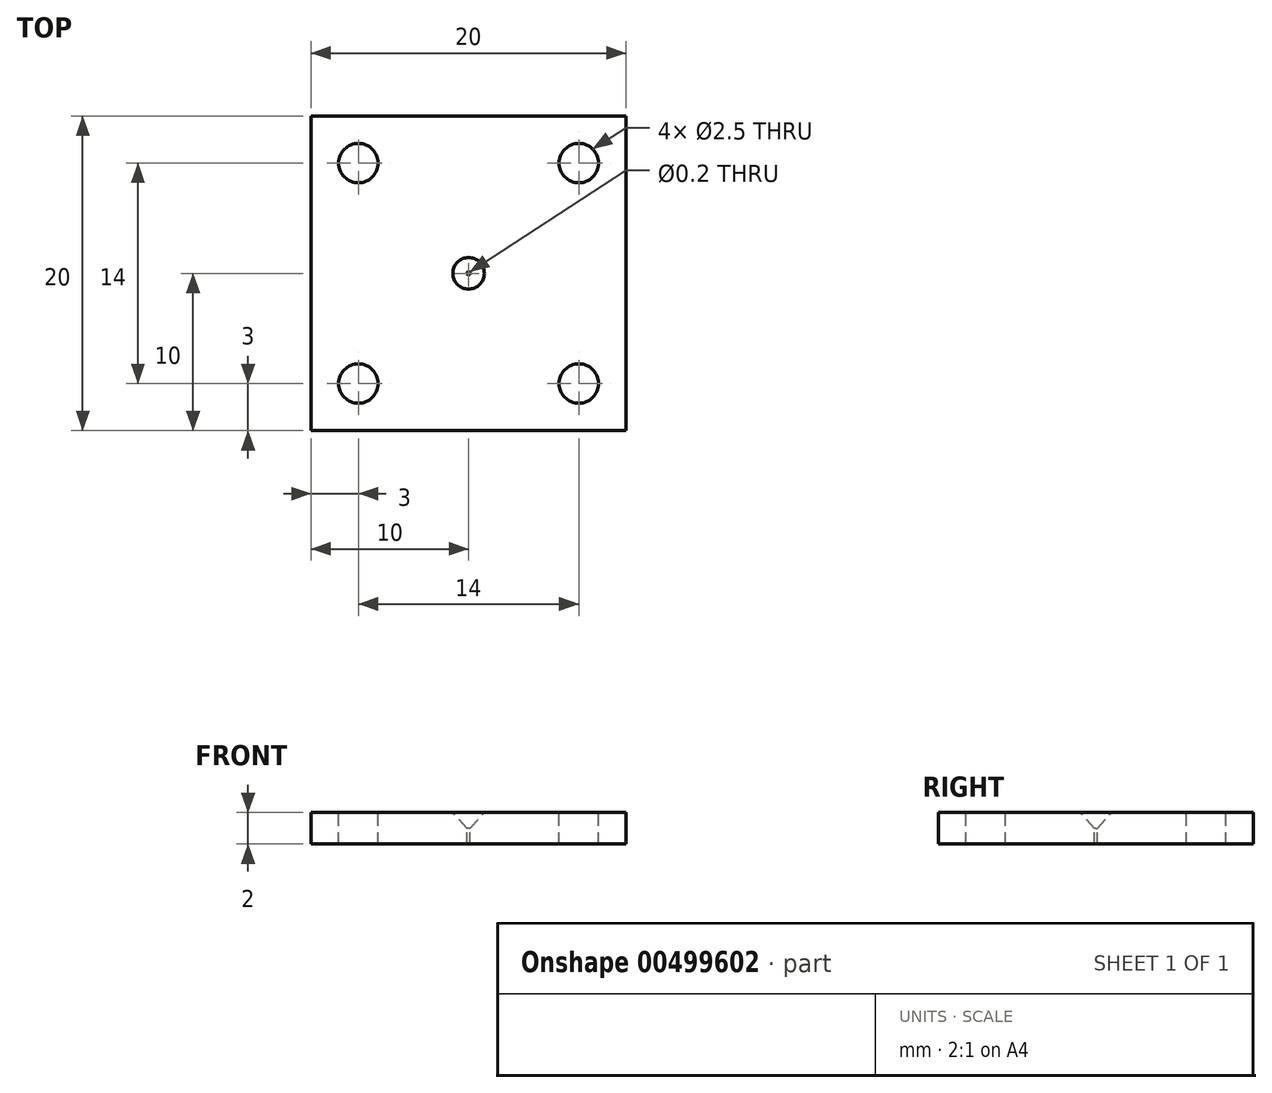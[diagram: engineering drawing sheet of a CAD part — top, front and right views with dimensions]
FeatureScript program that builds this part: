
annotation { "Feature Type Name" : "Feature", "Feature Type Description" : "" }
export const myFeature = defineFeature(function(context is Context, id is Id, definition is map)
    precondition{}
    {
        {
            var Q0;
            Q0=qCreatedBy(makeId("Top.planeOp"),FACE);
            var sketch = newSketch(context, id + "F0", { "sketchPlane" : qUnion([Q0])});
            skLineSegment(sketch, "E0.bottom", {"start": v(-10, 10) * mm, "end": v(10, 10) * mm});
            skLineSegment(sketch, "E0.top", {"start": v(-10, -10) * mm, "end": v(10, -10) * mm});
            skLineSegment(sketch, "E0.left", {"start": v(-10, 10) * mm, "end": v(-10, -10) * mm});
            skLineSegment(sketch, "E0.right", {"start": v(10, 10) * mm, "end": v(10, -10) * mm});
            skSolve(sketch);
        }
        {
            var Q0;
            Q0=makeQuery(id+"F0.imprint","IMPRINT",FACE,{"disambiguationData":[TD([[makeQuery(id+"F0.imprint","IMPRINT",EDGE,{"derivedFrom":sQuery(id+"F0.wireOp",EDGE,"E0.bottom")}),-1.0]])]});
            extrude(context, id + "F1", {"entities" : qUnion([Q0]), "oppositeDirection" : true, "depth" : 1 * mm});
        }
        {
            var Q0;
            Q0=makeQuery(id+"F1.opExtrude","CAP_FACE",FACE,{"disambiguationData":[OSD([sQuery(id+"F0.wireOp",EDGE,"E0.bottom"),sQuery(id+"F0.wireOp",EDGE,"E0.top"),sQuery(id+"F0.wireOp",EDGE,"E0.left"),sQuery(id+"F0.wireOp",EDGE,"E0.right")])],"isStart":true});
            var sketch = newSketch(context, id + "F2", { "sketchPlane" : qUnion([Q0])});
            skCircle(sketch, "E1", {"center": v(0, 0) * mm, "radius": 1 * mm});
            skSolve(sketch);
        }
        {
            var Q0;
            Q0=makeQuery(id+"F1.opExtrude","CAP_FACE",FACE,{"disambiguationData":[OSD([sQuery(id+"F0.wireOp",EDGE,"E0.bottom"),sQuery(id+"F0.wireOp",EDGE,"E0.top"),sQuery(id+"F0.wireOp",EDGE,"E0.left"),sQuery(id+"F0.wireOp",EDGE,"E0.right")])],"isStart":false});
            var sketch = newSketch(context, id + "F3", { "sketchPlane" : qUnion([Q0])});
            skCircle(sketch, "E2", {"center": v(0, 0) * mm, "radius": 0.1 * mm});
            skSolve(sketch);
        }
        {
            var Q1;
            Q1=makeQuery(id+"F2.imprint","IMPRINT",FACE,{"disambiguationData":[TD([[makeQuery(id+"F2.imprint","IMPRINT",EDGE,{"derivedFrom":sQuery(id+"F2.wireOp",EDGE,"E1")}),1.0]])]});
            var Q2;
            Q2=makeQuery(id+"F3.imprint","IMPRINT",FACE,{"disambiguationData":[TD([[makeQuery(id+"F3.imprint","IMPRINT",EDGE,{"derivedFrom":sQuery(id+"F3.wireOp",EDGE,"E2")}),1.0]])]});
            loft(context, id + "F4", {"operationType" : NewBodyOperationType.REMOVE, "sheetProfilesArray" : [{ "sheetProfileEntities" : qUnion([Q1]) }, { "sheetProfileEntities" : qUnion([Q2]) }]});
        }
        {
            var Q0;
            Q0=makeQuery(id+"F2.imprint","IMPRINT",FACE,{"disambiguationData":[TD([[makeQuery(id+"F2.imprint","IMPRINT",EDGE,{"derivedFrom":sQuery(id+"F2.wireOp",EDGE,"E1")}),-1.0]])]});
            var sketch = newSketch(context, id + "F5", { "sketchPlane" : qUnion([Q0])});
            skPoint(sketch, "E3", {"position": v(7, 7) * mm});
            skLineSegment(sketch, "E4", {"start": v(10.77, 0) * mm, "end": v(-10.68, 0) * mm});
            skLineSegment(sketch, "E5", {"start": v(0, -10.66) * mm, "end": v(0, 12.03) * mm});
            skPoint(sketch, "E6.MirrorP", {"position": v(-7, 7) * mm});
            skPoint(sketch, "E7.MirrorP", {"position": v(-7, -7) * mm});
            skPoint(sketch, "E8.MirrorP", {"position": v(7, -7) * mm});
            skSolve(sketch);
        }
        {
            var Q0;
            Q0=makeQuery(id+"F3.imprint","IMPRINT",FACE,{"disambiguationData":[TD([[makeQuery(id+"F3.imprint","IMPRINT",EDGE,{"derivedFrom":sQuery(id+"F3.wireOp",EDGE,"E2")}),-1.0]])]});
            var sketch = newSketch(context, id + "F6", { "sketchPlane" : qUnion([Q0])});
            skLineSegment(sketch, "E9.bottom", {"start": v(-10, 10) * mm, "end": v(10, 10) * mm});
            skLineSegment(sketch, "E9.top", {"start": v(-10, -10) * mm, "end": v(10, -10) * mm});
            skLineSegment(sketch, "E9.left", {"start": v(-10, 10) * mm, "end": v(-10, -10) * mm});
            skLineSegment(sketch, "E9.right", {"start": v(10, 10) * mm, "end": v(10, -10) * mm});
            skPoint(sketch, "E9.middle", {"position": v(0, 0) * mm});
            skCircle(sketch, "E10.0", {"center": v(0, 0) * mm, "radius": 0.1 * mm});
            skSolve(sketch);
        }
        {
            var Q0;
            Q0=makeQuery(id+"F6.imprint","IMPRINT",FACE,{"disambiguationData":[TD([[makeQuery(id+"F6.imprint","IMPRINT",EDGE,{"derivedFrom":sQuery(id+"F6.wireOp",EDGE,"E9.bottom")}),-1.0]])]});
            extrude(context, id + "F7", {"entities" : qUnion([Q0]), "operationType" : NewBodyOperationType.ADD, "depth" : 1 * mm});
        }
        {
            var Q0;
            Q0=sQuery(id+"F5.wireOp",VERTEX,"E7.MirrorP");
            var Q1;
            Q1=sQuery(id+"F5.wireOp",VERTEX,"E8.MirrorP");
            var Q2;
            Q2=sQuery(id+"F5.wireOp",VERTEX,"E3");
            var Q3;
            Q3=sQuery(id+"F5.wireOp",VERTEX,"E6.MirrorP");
            var Q4;
            Q4=makeQuery(id+"F1.opExtrude","SWEPT_BODY",BODY,{"disambiguationData":[OSD([sQuery(id+"F0.wireOp",EDGE,"E0.bottom"),sQuery(id+"F0.wireOp",EDGE,"E0.top"),sQuery(id+"F0.wireOp",EDGE,"E0.left"),sQuery(id+"F0.wireOp",EDGE,"E0.right")])]});
            hole(context, id + "F8", {"style" : HoleStyle.SIMPLE, "endStyle" : HoleEndStyle.THROUGH, "standardTappedOrClearance" : lookupTablePath({ "standard" : "ISO", "engagement" : "75%", "pitch" : "0.5 mm", "size" : "M3", "type" : "Tapped" }), "standardBlindInLast" : lookupTablePath({ "standard" : "ISO", "engagement" : "75%", "pitch" : "0.5 mm", "size" : "M3", "type" : "Tapped" }), "holeDiameter" : 2.5 * mm, "showTappedDepth" : true, "isTappedThrough" : true, "tappedDepth" : 12 * mm, "tapClearance" : 3, "startFromSketch" : true, "locations" : qUnion([Q0, Q1, Q2, Q3]), "scope" : qUnion([Q4]), "majorDiameter" : 3 * mm});
        }
    });
